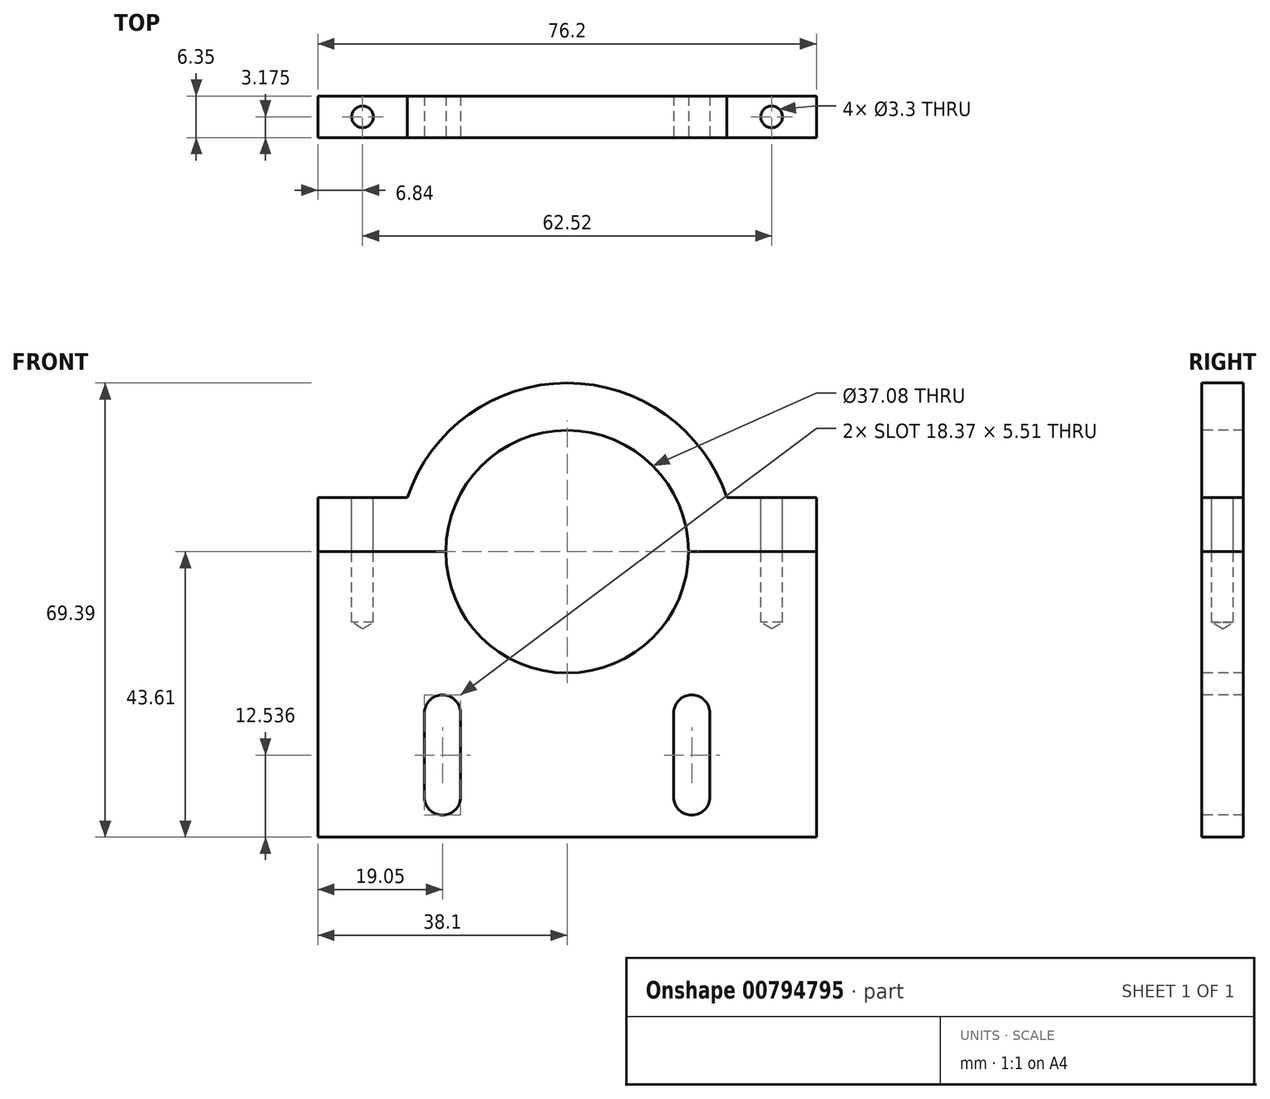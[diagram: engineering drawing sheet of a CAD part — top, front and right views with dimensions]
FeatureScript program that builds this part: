
annotation { "Feature Type Name" : "Feature", "Feature Type Description" : "" }
export const myFeature = defineFeature(function(context is Context, id is Id, definition is map)
    precondition{}
    {
        {
            var Q0;
            Q0=qCreatedBy(makeId("Front.planeOp"),FACE);
            var sketch = newSketch(context, id + "F0", { "sketchPlane" : qUnion([Q0])});
            skLineSegment(sketch, "E0.top", {"start": v(-38.1, -43.6) * mm, "end": v(38.1, -43.6) * mm});
            skLineSegment(sketch, "E0.left", {"start": v(-38.1, 8.27) * mm, "end": v(-38.1, -43.6) * mm});
            skLineSegment(sketch, "E0.right", {"start": v(38.1, 8.27) * mm, "end": v(38.1, -43.6) * mm});
            skPoint(sketch, "E0.middle", {"position": v(0, 0) * mm});
            skCircle(sketch, "E1", {"center": v(0, 0) * mm, "radius": 18.54 * mm});
            skLineSegment(sketch, "E2", {"start": v(-38.1, 0) * mm, "end": v(38.1, 0) * mm});
            skArc(sketch, "E3", {"start": v(24.42, 8.27) * mm, "mid": v(0, 25.78) * mm, "end": v(-24.42, 8.27) * mm});
            skLineSegment(sketch, "E4", {"start": v(24.42, 8.27) * mm, "end": v(38.1, 8.27) * mm});
            skLineSegment(sketch, "E5", {"start": v(-24.42, 8.27) * mm, "end": v(-38.1, 8.27) * mm});
            skPoint(sketch, "E6", {"position": v(0, 18.54) * mm});
            skPoint(sketch, "E7", {"position": v(18.54, 0) * mm});
            skPoint(sketch, "E8", {"position": v(-18.54, 0) * mm});
            skPoint(sketch, "E9.startSnap0", {"position": v(0, -31.07) * mm});
            skArc(sketch, "E10", {"start": v(2.76, -24.65) * mm, "mid": v(0, -21.89) * mm, "end": v(-2.76, -24.65) * mm});
            skArc(sketch, "E11.MirrorC", {"start": v(2.76, -37.5) * mm, "mid": v(0, -40.26) * mm, "end": v(-2.76, -37.5) * mm});
            skLineSegment(sketch, "E12", {"start": v(-2.76, -24.65) * mm, "end": v(-2.76, -37.5) * mm});
            skLineSegment(sketch, "E13", {"start": v(2.76, -24.65) * mm, "end": v(2.76, -37.5) * mm});
            skLineSegment(sketch, "E14", {"start": v(0, -43.6) * mm, "end": v(-38.1, -43.6) * mm});
            skPoint(sketch, "E15", {"position": v(-19.05, -43.6) * mm});
            skLineSegment(sketch, "E16", {"start": v(0, -43.6) * mm, "end": v(38.1, -43.6) * mm});
            skPoint(sketch, "E17", {"position": v(19.05, -43.6) * mm});
            skLineSegment(sketch, "E18", {"start": v(19.05, -43.6) * mm, "end": v(19.05, -27.4) * mm});
            skCircle(sketch, "E19", {"center": v(19.05, -24.65) * mm, "radius": 2.76 * mm});
            skCircle(sketch, "E20", {"center": v(19.05, -37.5) * mm, "radius": 2.76 * mm});
            skLineSegment(sketch, "E21", {"start": v(16.3, -24.65) * mm, "end": v(16.3, -37.5) * mm});
            skLineSegment(sketch, "E22", {"start": v(21.8, -24.65) * mm, "end": v(21.8, -37.5) * mm});
            skCircle(sketch, "E23.MirrorC", {"center": v(-19.05, -24.65) * mm, "radius": 2.76 * mm});
            skCircle(sketch, "E24.MirrorC", {"center": v(-19.05, -37.5) * mm, "radius": 2.76 * mm});
            skLineSegment(sketch, "E25.MirrorCS", {"start": v(-21.8, -24.65) * mm, "end": v(-21.8, -37.5) * mm});
            skLineSegment(sketch, "E26.MirrorCS", {"start": v(-16.3, -24.65) * mm, "end": v(-16.3, -37.5) * mm});
            skSolve(sketch);
        }
        {
            var Q0;
            {var subQ5=sQuery(id+"F0.wireOp",EDGE,"E0.top");Q0=makeQuery(id+"F0.imprint","IMPRINT",FACE,{"disambiguationData":[TD([[makeQuery(id+"F0.imprint","IMPRINT",EDGE,{"derivedFrom":subQ5}),1.0]])]});}
            var Q1;
            {var subQ0=sQuery(id+"F0.wireOp",EDGE,"E9");Q1=makeQuery(id+"F0.imprint","IMPRINT",FACE,{"disambiguationData":[TD([[makeQuery(id+"F0.imprint","IMPRINT",EDGE,{"derivedFrom":subQ0}),1.0]])]});}
            var Q2;
            {var subQ0=sQuery(id+"F0.wireOp",EDGE,"87JciAUj-Zg7c-dX8n-6LIc-esLXFlYuvTSq");Q2=makeQuery(id+"F0.imprint","IMPRINT",FACE,{"disambiguationData":[TD([[makeQuery(id+"F0.imprint","IMPRINT",EDGE,{"derivedFrom":subQ0}),1.0]])]});}
            var Q3;
            {var subQ6=sQuery(id+"F0.wireOp",EDGE,"E10");Q3=makeQuery(id+"F0.imprint","IMPRINT",FACE,{"disambiguationData":[TD([[makeQuery(id+"F0.imprint","IMPRINT",EDGE,{"derivedFrom":subQ6}),-1.0]])]});}
            var Q4;
            {var subQ16=sQuery(id+"F0.wireOp",EDGE,"E11.MirrorC");Q4=makeQuery(id+"F0.imprint","IMPRINT",FACE,{"disambiguationData":[TD([[makeQuery(id+"F0.imprint","IMPRINT",EDGE,{"derivedFrom":subQ16}),1.0]])]});}
            var Q5;
            {var subQ0=sQuery(id+"F0.wireOp",EDGE,"E16");var subQ1=sQuery(id+"F0.wireOp",EDGE,"E0.right");var subQ2=makeQuery(id+"F0.imprint","INTERSECT",VERTEX,{"derivedFrom":[subQ1,subQ0]});Q5=makeQuery(id+"F0.imprint","IMPRINT",FACE,{"disambiguationData":[TD([[makeQuery(id+"F0.imprint","IMPRINT",EDGE,{"disambiguationData":[TD([[subQ2,1.0]])],"derivedFrom":subQ1}),-1.0]])]});}
            extrude(context, id + "F1", {"entities" : qUnion([Q0, Q1, Q2, Q3, Q4, Q5]), "oppositeDirection" : true, "depth" : 6.35 * mm, "offsetDistance" : 25.4 * mm});
        }
        {
            var Q0;
            Q0=makeQuery(id+"F0.imprint","IMPRINT",FACE,{"disambiguationData":[TD([[makeQuery(id+"F0.imprint","IMPRINT",EDGE,{"derivedFrom":sQuery(id+"F0.wireOp",EDGE,"E3")}),1.0]])]});
            extrude(context, id + "F2", {"entities" : qUnion([Q0]), "oppositeDirection" : true, "depth" : 6.35 * mm, "offsetDistance" : 25.4 * mm});
        }
        {
            var Q0;
            Q0=makeQuery(id+"F2.opExtrude","SWEPT_FACE",FACE,{"disambiguationData":[OSD([sQuery(id+"F0.wireOp",EDGE,"E5")])]});
            var sketch = newSketch(context, id + "F3", { "sketchPlane" : qUnion([Q0])});
            skPoint(sketch, "E27", {"position": v(-31.26, 3.18) * mm});
            skPoint(sketch, "E27.positionSnap0", {"position": v(-38.1, 3.18) * mm});
            skPoint(sketch, "E27.positionSnap1", {"position": v(-31.26, 6.35) * mm});
            skSolve(sketch);
        }
        {
            var Q0;
            Q0=makeQuery(id+"F2.opExtrude","SWEPT_FACE",FACE,{"disambiguationData":[OSD([sQuery(id+"F0.wireOp",EDGE,"E4")])]});
            var sketch = newSketch(context, id + "F4", { "sketchPlane" : qUnion([Q0])});
            skPoint(sketch, "E28", {"position": v(31.26, 3.18) * mm});
            skPoint(sketch, "E28.positionSnap0", {"position": v(38.1, 3.18) * mm});
            skPoint(sketch, "E28.positionSnap1", {"position": v(31.26, 6.35) * mm});
            skSolve(sketch);
        }
        {
            var Q0;
            Q0=sQuery(id+"F3.wireOp",VERTEX,"E27");
            var Q1;
            Q1=sQuery(id+"F4.wireOp",VERTEX,"E28");
            var Q2;
            Q2=makeQuery(id+"F1.opExtrude","SWEPT_BODY",BODY,{"disambiguationData":[OSD([sQuery(id+"F0.wireOp",EDGE,"E0.top"),sQuery(id+"F0.wireOp",EDGE,"E0.left"),sQuery(id+"F0.wireOp",EDGE,"E0.right"),sQuery(id+"F0.wireOp",EDGE,"E1"),sQuery(id+"F0.wireOp",EDGE,"E2")])]});
            var Q3;
            Q3=makeQuery(id+"F2.opExtrude","SWEPT_BODY",BODY,{"disambiguationData":[OSD([sQuery(id+"F0.wireOp",EDGE,"E0.left"),sQuery(id+"F0.wireOp",EDGE,"E0.right"),sQuery(id+"F0.wireOp",EDGE,"E1"),sQuery(id+"F0.wireOp",EDGE,"E2"),sQuery(id+"F0.wireOp",EDGE,"E3"),sQuery(id+"F0.wireOp",EDGE,"E4"),sQuery(id+"F0.wireOp",EDGE,"E5")])]});
            hole(context, id + "F5", {"style" : HoleStyle.SIMPLE, "endStyle" : HoleEndStyle.BLIND, "standardTappedOrClearance" : lookupTablePath({ "standard" : "ISO", "engagement" : "75%", "pitch" : "0.7 mm", "size" : "M4", "type" : "Tapped" }), "standardBlindInLast" : lookupTablePath({ "standard" : "ISO", "engagement" : "75%", "pitch" : "0.7 mm", "size" : "M4", "type" : "Tapped" }), "holeDiameter" : 3.3 * mm, "majorDiameter" : 4 * mm, "showTappedDepth" : true, "holeDepth" : 19.05 * mm, "isTappedThrough" : true, "tappedDepth" : 16.95 * mm, "tapClearance" : 3, "startFromSketch" : true, "locations" : qUnion([Q0, Q1]), "scope" : qUnion([Q2, Q3])});
        }
    });
